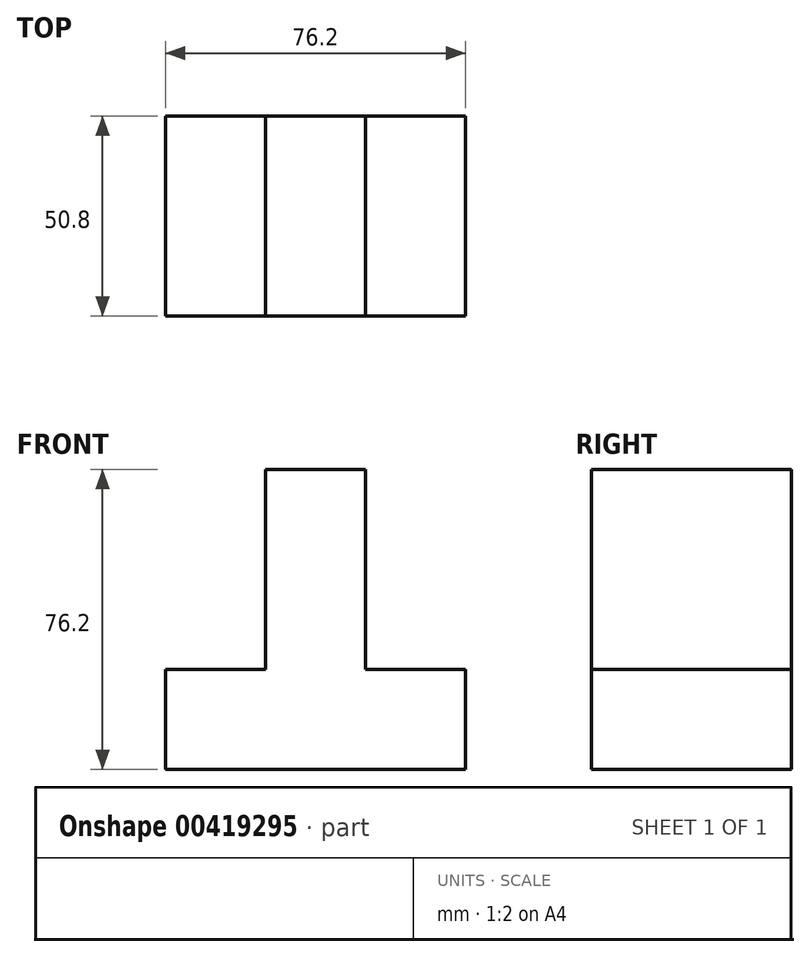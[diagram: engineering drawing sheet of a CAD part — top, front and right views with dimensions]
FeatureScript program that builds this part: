
annotation { "Feature Type Name" : "Feature", "Feature Type Description" : "" }
export const myFeature = defineFeature(function(context is Context, id is Id, definition is map)
    precondition{}
    {
        {
            var Q0;
            Q0=qCreatedBy(makeId("Front.planeOp"),FACE);
            var sketch = newSketch(context, id + "F0", { "sketchPlane" : qUnion([Q0])});
            skLineSegment(sketch, "E0", {"start": v(-44.1, -9.4) * mm, "end": v(-44.1, 16) * mm});
            skLineSegment(sketch, "E1", {"start": v(-44.1, 16) * mm, "end": v(-18.7, 16) * mm});
            skLineSegment(sketch, "E2", {"start": v(-18.7, 16) * mm, "end": v(-18.7, 66.8) * mm});
            skLineSegment(sketch, "E3", {"start": v(-18.7, 66.8) * mm, "end": v(6.7, 66.8) * mm});
            skLineSegment(sketch, "E4", {"start": v(6.7, 66.8) * mm, "end": v(6.7, 16) * mm});
            skLineSegment(sketch, "E5", {"start": v(6.7, 16) * mm, "end": v(32.1, 16) * mm});
            skLineSegment(sketch, "E6", {"start": v(32.1, 16) * mm, "end": v(32.1, -9.4) * mm});
            skLineSegment(sketch, "E7", {"start": v(32.1, -9.4) * mm, "end": v(-44.1, -9.4) * mm});
            skSolve(sketch);
        }
        {
            var Q0;
            Q0 = qSketchRegion(id + "F0", true);
            extrude(context, id + "F1", {"entities" : qUnion([Q0]), "depth" : 50.8 * mm});
        }
    });
